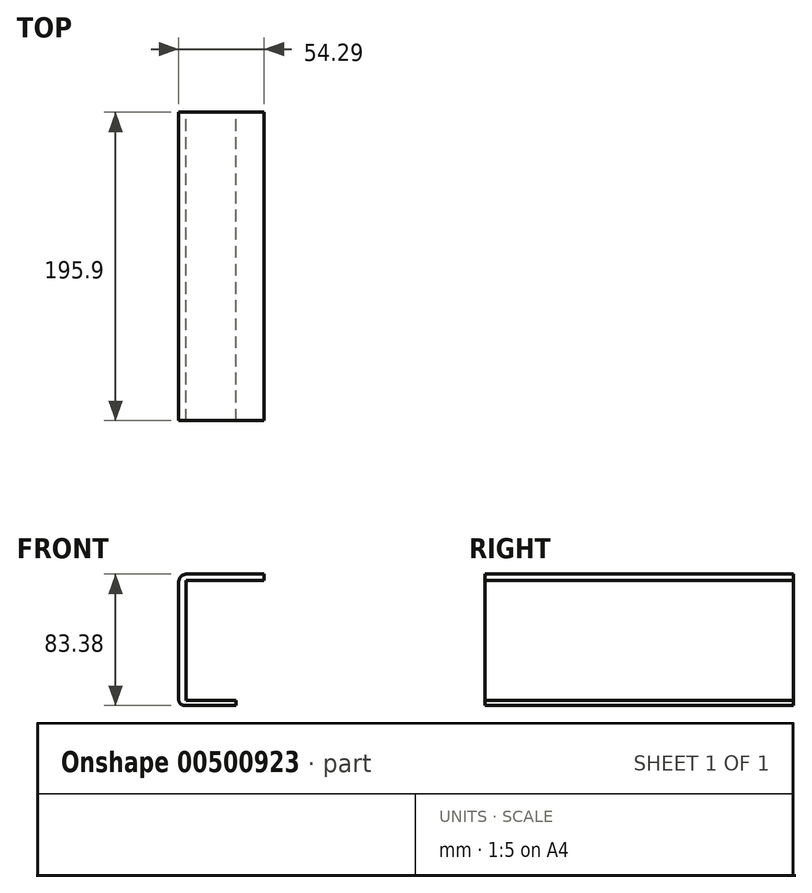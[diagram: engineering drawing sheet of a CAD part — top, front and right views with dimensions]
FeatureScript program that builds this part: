
annotation { "Feature Type Name" : "Feature", "Feature Type Description" : "" }
export const myFeature = defineFeature(function(context is Context, id is Id, definition is map)
    precondition{}
    {
        {
            var Q0;
            Q0=qCreatedBy(makeId("Right.planeOp"),FACE);
            var sketch = newSketch(context, id + "F0", { "sketchPlane" : qUnion([Q0])});
            skLineSegment(sketch, "E0.bottom", {"start": v(-97.95, 41.7) * mm, "end": v(97.95, 41.7) * mm});
            skLineSegment(sketch, "E0.top", {"start": v(-97.95, -41.7) * mm, "end": v(97.95, -41.7) * mm});
            skLineSegment(sketch, "E0.left", {"start": v(-97.95, 41.7) * mm, "end": v(-97.95, -41.7) * mm});
            skLineSegment(sketch, "E0.right", {"start": v(97.95, 41.7) * mm, "end": v(97.95, -41.7) * mm});
            skPoint(sketch, "E0.middle", {"position": v(0, 0) * mm});
            skSolve(sketch);
        }
        {
            var Q0;
            Q0=makeQuery(id+"F0.imprint","IMPRINT",FACE,{"disambiguationData":[TD([[makeQuery(id+"F0.imprint","IMPRINT",EDGE,{"derivedFrom":sQuery(id+"F0.wireOp",EDGE,"E0.bottom")}),-1.0]])]});
            extrude(context, id + "F1", {"entities" : qUnion([Q0]), "depth" : 4.76 * mm});
        }
        {
            var Q0;
            Q0=makeQuery(id+"F1.opExtrude","CAP_FACE",FACE,{"disambiguationData":[OSD([sQuery(id+"F0.wireOp",EDGE,"E0.bottom"),sQuery(id+"F0.wireOp",EDGE,"E0.top"),sQuery(id+"F0.wireOp",EDGE,"E0.left"),sQuery(id+"F0.wireOp",EDGE,"E0.right")])],"isStart":false});
            var sketch = newSketch(context, id + "F2", { "sketchPlane" : qUnion([Q0])});
            skLineSegment(sketch, "E1.bottom", {"start": v(-97.95, -41.7) * mm, "end": v(97.95, -41.7) * mm});
            skLineSegment(sketch, "E1.top", {"start": v(-97.95, -38.45) * mm, "end": v(97.95, -38.45) * mm});
            skLineSegment(sketch, "E1.left", {"start": v(-97.95, -41.7) * mm, "end": v(-97.95, -38.45) * mm});
            skLineSegment(sketch, "E1.right", {"start": v(97.95, -41.7) * mm, "end": v(97.95, -38.45) * mm});
            skSolve(sketch);
        }
        {
            var Q0;
            Q0=makeQuery(id+"F2.imprint","IMPRINT",FACE,{"disambiguationData":[TD([[makeQuery(id+"F2.imprint","IMPRINT",EDGE,{"derivedFrom":sQuery(id+"F2.wireOp",EDGE,"E1.bottom")}),1.0]])]});
            extrude(context, id + "F3", {"entities" : qUnion([Q0]), "operationType" : NewBodyOperationType.ADD, "depth" : 34.85 * mm});
        }
        {
            var Q0;
            Q0=makeQuery(id+"F1.opExtrude","CAP_EDGE",EDGE,{"disambiguationData":[OSD([sQuery(id+"F0.wireOp",EDGE,"E0.top")])],"isStart":true});
            fillet(context, id + "F4", {"entities" : qUnion([Q0]), "radius" : 3.68 * mm, "tangentPropagation" : true, "allowEdgeOverflow" : false});
        }
        {
            var Q0;
            Q0=makeQuery(id+"F3.opExtrude","CAP_FACE",FACE,{"disambiguationData":[OSD([sQuery(id+"F2.wireOp",EDGE,"E1.bottom"),sQuery(id+"F2.wireOp",EDGE,"E1.top"),sQuery(id+"F2.wireOp",EDGE,"E1.left"),sQuery(id+"F2.wireOp",EDGE,"E1.right")])],"isStart":false});
            extrude(context, id + "F5", {"entities" : qUnion([Q0]), "operationType" : NewBodyOperationType.REMOVE, "oppositeDirection" : true, "depth" : 3.17 * mm});
        }
        {
            var Q0;
            Q0=makeQuery(id+"F1.opExtrude","CAP_FACE",FACE,{"disambiguationData":[OSD([sQuery(id+"F0.wireOp",EDGE,"E0.bottom"),sQuery(id+"F0.wireOp",EDGE,"E0.top"),sQuery(id+"F0.wireOp",EDGE,"E0.left"),sQuery(id+"F0.wireOp",EDGE,"E0.right")])],"isStart":false});
            var sketch = newSketch(context, id + "F6", { "sketchPlane" : qUnion([Q0])});
            skLineSegment(sketch, "E2.bottom", {"start": v(-97.95, 41.7) * mm, "end": v(97.95, 41.7) * mm});
            skLineSegment(sketch, "E2.top", {"start": v(-97.95, 37.64) * mm, "end": v(97.95, 37.64) * mm});
            skLineSegment(sketch, "E2.left", {"start": v(-97.95, 41.7) * mm, "end": v(-97.95, 37.64) * mm});
            skLineSegment(sketch, "E2.right", {"start": v(97.95, 41.7) * mm, "end": v(97.95, 37.64) * mm});
            skSolve(sketch);
        }
        {
            var Q0;
            Q0=makeQuery(id+"F6.imprint","IMPRINT",FACE,{"disambiguationData":[TD([[makeQuery(id+"F6.imprint","IMPRINT",EDGE,{"derivedFrom":sQuery(id+"F6.wireOp",EDGE,"E2.bottom")}),-1.0]])]});
            extrude(context, id + "F7", {"entities" : qUnion([Q0]), "operationType" : NewBodyOperationType.ADD, "depth" : 49.53 * mm});
        }
        {
            var Q0;
            Q0=makeQuery(id+"F1.opExtrude","CAP_EDGE",EDGE,{"disambiguationData":[OSD([sQuery(id+"F0.wireOp",EDGE,"E0.bottom")])],"isStart":true});
            fillet(context, id + "F8", {"entities" : qUnion([Q0]), "radius" : 5.08 * mm, "tangentPropagation" : true, "allowEdgeOverflow" : false});
        }
    });
